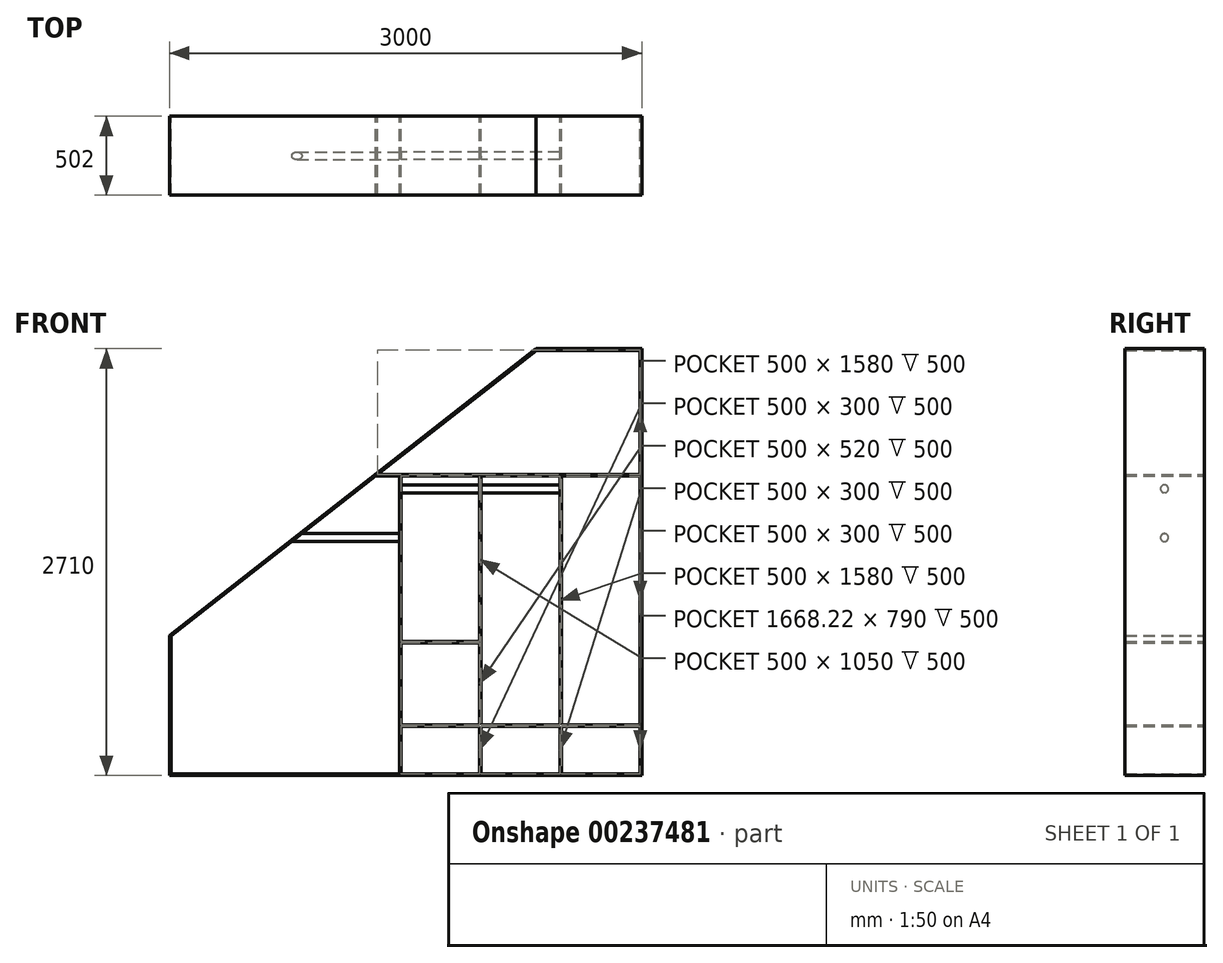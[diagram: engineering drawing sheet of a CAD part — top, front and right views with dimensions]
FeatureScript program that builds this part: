
annotation { "Feature Type Name" : "Feature", "Feature Type Description" : "" }
export const myFeature = defineFeature(function(context is Context, id is Id, definition is map)
    precondition{}
    {
        {
            var Q0;
            Q0=qCreatedBy(makeId("Front.planeOp"),FACE);
            var sketch = newSketch(context, id + "F0", { "sketchPlane" : qUnion([Q0])});
            skLineSegment(sketch, "E0", {"start": v(0, 0) * mm, "end": v(3000, 0) * mm});
            skLineSegment(sketch, "E1", {"start": v(3000, 0) * mm, "end": v(3000, 2710) * mm});
            skLineSegment(sketch, "E2", {"start": v(3000, 2710) * mm, "end": v(2329.5, 2710) * mm});
            skLineSegment(sketch, "E3", {"start": v(2329.5, 2710) * mm, "end": v(0, 890) * mm});
            skLineSegment(sketch, "E4", {"start": v(0, 890) * mm, "end": v(0, 0) * mm});
            skLineSegment(sketch, "E5.0", {"start": v(10, 885.12) * mm, "end": v(10, 10) * mm});
            skLineSegment(sketch, "E5.1", {"start": v(2332.94, 2700) * mm, "end": v(1321.78, 1910) * mm});
            skLineSegment(sketch, "E5.2", {"start": v(10, 10) * mm, "end": v(1460, 10) * mm});
            skLineSegment(sketch, "E5.3", {"start": v(2990, 10) * mm, "end": v(2990, 1900) * mm});
            skLineSegment(sketch, "E5.4", {"start": v(2990, 2700) * mm, "end": v(2332.94, 2700) * mm});
            skLineSegment(sketch, "E6", {"start": v(1036.75, 0) * mm, "end": v(1036.75, 1700) * mm, "construction": true});
            skLineSegment(sketch, "E7", {"start": v(1321.78, 1910) * mm, "end": v(2990, 1910) * mm});
            skLineSegment(sketch, "E8", {"start": v(2990, 1900) * mm, "end": v(2490, 1900) * mm});
            skLineSegment(sketch, "E9", {"start": v(2490, 1900) * mm, "end": v(2490, 320) * mm});
            skLineSegment(sketch, "E10", {"start": v(2480, 10) * mm, "end": v(2480, 310) * mm});
            skLineSegment(sketch, "E11", {"start": v(1970, 1900) * mm, "end": v(1970, 850) * mm});
            skLineSegment(sketch, "E12", {"start": v(1980, 1900) * mm, "end": v(1980, 320) * mm});
            skLineSegment(sketch, "E13", {"start": v(1470, 1900) * mm, "end": v(1470, 850) * mm});
            skLineSegment(sketch, "E14", {"start": v(1460, 1900) * mm, "end": v(1460, 10) * mm});
            skLineSegment(sketch, "E15.bottom", {"start": v(1470, 320) * mm, "end": v(1970, 320) * mm});
            skLineSegment(sketch, "E15.top", {"start": v(1470, 310) * mm, "end": v(1970, 310) * mm});
            skLineSegment(sketch, "E15.left", {"start": v(1470, 320) * mm, "end": v(1470, 310) * mm});
            skLineSegment(sketch, "E16.bottom", {"start": v(1470, 850) * mm, "end": v(1970, 850) * mm});
            skLineSegment(sketch, "E16.top", {"start": v(1470, 840) * mm, "end": v(1970, 840) * mm});
            skLineSegment(sketch, "E17.trimOffspring", {"start": v(1308.98, 1900) * mm, "end": v(10, 885.12) * mm});
            skLineSegment(sketch, "E18.trimOffspring", {"start": v(1460, 1900) * mm, "end": v(1308.98, 1900) * mm});
            skLineSegment(sketch, "E19.trimOffspring", {"start": v(1970, 1900) * mm, "end": v(1470, 1900) * mm});
            skLineSegment(sketch, "E20.trimOffspring", {"start": v(2480, 1900) * mm, "end": v(1980, 1900) * mm});
            skLineSegment(sketch, "E21.trimOffspring", {"start": v(2990, 1910) * mm, "end": v(2990, 2700) * mm});
            skLineSegment(sketch, "E22.trimOffspring", {"start": v(1470, 840) * mm, "end": v(1470, 10) * mm});
            skLineSegment(sketch, "E23.trimOffspring", {"start": v(1970, 840) * mm, "end": v(1970, 320) * mm});
            skLineSegment(sketch, "E24.trimOffspring", {"start": v(2490, 310) * mm, "end": v(2490, 10) * mm});
            skLineSegment(sketch, "E25.trimOffspring", {"start": v(2490, 320) * mm, "end": v(2990, 320) * mm});
            skLineSegment(sketch, "E26.trimOffspring", {"start": v(2480, 320) * mm, "end": v(2480, 1900) * mm});
            skLineSegment(sketch, "E27.trimOffspring", {"start": v(2490, 310) * mm, "end": v(2990, 310) * mm});
            skLineSegment(sketch, "E28.trimOffspring", {"start": v(1980, 320) * mm, "end": v(2480, 320) * mm});
            skLineSegment(sketch, "E29.trimOffspring", {"start": v(1980, 310) * mm, "end": v(2480, 310) * mm});
            skLineSegment(sketch, "E30.trimOffspring", {"start": v(1970, 310) * mm, "end": v(1970, 10) * mm});
            skLineSegment(sketch, "E31.trimOffspring", {"start": v(1980, 310) * mm, "end": v(1980, 10) * mm});
            skLineSegment(sketch, "E32.trimOffspring", {"start": v(2490, 10) * mm, "end": v(2990, 10) * mm});
            skLineSegment(sketch, "E33.trimOffspring", {"start": v(1980, 10) * mm, "end": v(2480, 10) * mm});
            skLineSegment(sketch, "E34.trimOffspring", {"start": v(1470, 10) * mm, "end": v(1970, 10) * mm});
            skSolve(sketch);
        }
        {
            var Q0;
            Q0=makeQuery(id+"F0.imprint","IMPRINT",FACE,{"disambiguationData":[TD([[makeQuery(id+"F0.imprint","IMPRINT",EDGE,{"derivedFrom":sQuery(id+"F0.wireOp",EDGE,"E0")}),1.0]])]});
            extrude(context, id + "F1", {"entities" : qUnion([Q0]), "depth" : 500 * mm});
        }
        {
            var Q0;
            Q0=makeQuery(id+"F0.imprint","IMPRINT",FACE,{"disambiguationData":[TD([[makeQuery(id+"F0.imprint","IMPRINT",EDGE,{"derivedFrom":sQuery(id+"F0.wireOp",EDGE,"E5.0")}),1.0]])]});
            var Q1;
            Q1=makeQuery(id+"F0.imprint","IMPRINT",FACE,{"disambiguationData":[TD([[makeQuery(id+"F0.imprint","IMPRINT",EDGE,{"derivedFrom":sQuery(id+"F0.wireOp",EDGE,"E0")}),1.0]])]});
            var Q2;
            {var subQ3=sQuery(id+"F0.wireOp",EDGE,"E9");Q2=makeQuery(id+"F0.imprint","IMPRINT",FACE,{"disambiguationData":[TD([[makeQuery(id+"F0.imprint","IMPRINT",EDGE,{"derivedFrom":subQ3}),1.0]])]});}
            var Q3;
            {var subQ0=sQuery(id+"F0.wireOp",EDGE,"E5.4");Q3=makeQuery(id+"F0.imprint","IMPRINT",FACE,{"disambiguationData":[TD([[makeQuery(id+"F0.imprint","IMPRINT",EDGE,{"derivedFrom":subQ0}),1.0]])]});}
            var Q4;
            {var subQ0=sQuery(id+"F0.wireOp",EDGE,"E11");Q4=makeQuery(id+"F0.imprint","IMPRINT",FACE,{"disambiguationData":[TD([[makeQuery(id+"F0.imprint","IMPRINT",EDGE,{"derivedFrom":subQ0}),1.0]])]});}
            var Q5;
            Q5=makeQuery(id+"F0.imprint","IMPRINT",FACE,{"disambiguationData":[TD([[makeQuery(id+"F0.imprint","IMPRINT",EDGE,{"derivedFrom":sQuery(id+"F0.wireOp",EDGE,"E7")}),-1.0]])]});
            var Q6;
            {var subQ0=sQuery(id+"F0.wireOp",EDGE,"E9");Q6=makeQuery(id+"F0.imprint","IMPRINT",FACE,{"disambiguationData":[TD([[makeQuery(id+"F0.imprint","IMPRINT",EDGE,{"derivedFrom":subQ0}),-1.0]])]});}
            var Q7;
            {var subQ0=sQuery(id+"F0.wireOp",EDGE,"E11");Q7=makeQuery(id+"F0.imprint","IMPRINT",FACE,{"disambiguationData":[TD([[makeQuery(id+"F0.imprint","IMPRINT",EDGE,{"derivedFrom":subQ0}),-1.0]])]});}
            var Q8;
            {var subQ0=sQuery(id+"F0.wireOp",EDGE,"E13");Q8=makeQuery(id+"F0.imprint","IMPRINT",FACE,{"disambiguationData":[TD([[makeQuery(id+"F0.imprint","IMPRINT",EDGE,{"derivedFrom":subQ0}),-1.0]])]});}
            var Q9;
            Q9=makeQuery(id+"F0.imprint","IMPRINT",FACE,{"disambiguationData":[TD([[makeQuery(id+"F0.imprint","IMPRINT",EDGE,{"derivedFrom":sQuery(id+"F0.wireOp",EDGE,"E12")}),1.0]])]});
            var Q10;
            Q10=makeQuery(id+"F0.imprint","IMPRINT",FACE,{"disambiguationData":[TD([[makeQuery(id+"F0.imprint","IMPRINT",EDGE,{"derivedFrom":sQuery(id+"F0.wireOp",EDGE,"E24.trimOffspring")}),1.0]])]});
            var Q11;
            Q11=makeQuery(id+"F0.imprint","IMPRINT",FACE,{"disambiguationData":[TD([[makeQuery(id+"F0.imprint","IMPRINT",EDGE,{"derivedFrom":sQuery(id+"F0.wireOp",EDGE,"E10")}),1.0]])]});
            var Q12;
            {var subQ0=sQuery(id+"F0.wireOp",EDGE,"E15.top");Q12=makeQuery(id+"F0.imprint","IMPRINT",FACE,{"disambiguationData":[TD([[makeQuery(id+"F0.imprint","IMPRINT",EDGE,{"derivedFrom":subQ0}),-1.0]])]});}
            var Q13;
            {var subQ0=sQuery(id+"F0.wireOp",EDGE,"E15.bottom");Q13=makeQuery(id+"F0.imprint","IMPRINT",FACE,{"disambiguationData":[TD([[makeQuery(id+"F0.imprint","IMPRINT",EDGE,{"derivedFrom":subQ0}),1.0]])]});}
            extrude(context, id + "F2", {"entities" : qUnion([Q0, Q1, Q2, Q3, Q4, Q5, Q6, Q7, Q8, Q9, Q10, Q11, Q12, Q13]), "operationType" : NewBodyOperationType.ADD, "oppositeDirection" : true, "depth" : 2 * mm});
        }
        {
            var Q0;
            {var subQ0=sQuery(id+"F0.wireOp",EDGE,"E13");Q0=makeQuery(id+"F1.opExtrude","SWEPT_FACE",FACE,{"disambiguationData":[OSD([subQ0]),TDD([makeQuery(id+"F0.imprint","IMPRINT",EDGE,{"disambiguationData":[TD([[makeQuery(id+"F0.imprint","INTERSECT",VERTEX,{"derivedFrom":[sQuery(id+"F0.wireOp",EDGE,"E8"),subQ0]}),-1.0]])],"derivedFrom":subQ0})])]});}
            var sketch = newSketch(context, id + "F3", { "sketchPlane" : qUnion([Q0])});
            skCircle(sketch, "E35", {"center": v(-250, 1820) * mm, "radius": 25 * mm});
            skSolve(sketch);
        }
        {
            var Q0;
            Q0=makeQuery(id+"F3.imprint","IMPRINT",FACE,{"disambiguationData":[TD([[makeQuery(id+"F3.imprint","IMPRINT",EDGE,{"derivedFrom":sQuery(id+"F3.wireOp",EDGE,"E35")}),1.0]])]});
            var Q1;
            {var subQ0=sQuery(id+"F0.wireOp",EDGE,"E10");Q1=makeQuery(id+"F1.opExtrude","SWEPT_FACE",FACE,{"disambiguationData":[OSD([subQ0]),TDD([makeQuery(id+"F0.imprint","IMPRINT",EDGE,{"disambiguationData":[TD([[makeQuery(id+"F0.imprint","INTERSECT",VERTEX,{"derivedFrom":[sQuery(id+"F0.wireOp",EDGE,"E8"),subQ0]}),1.0]])],"derivedFrom":subQ0})])]});}
            extrude(context, id + "F4", {"entities" : qUnion([Q0]), "operationType" : NewBodyOperationType.ADD, "endBound" : BoundingType.UP_TO_SURFACE, "endBoundEntityFace" : qUnion([Q1]), "depth" : 25 * mm});
        }
        {
            var Q0;
            Q0=makeQuery(id+"F1.opExtrude","SWEPT_FACE",FACE,{"disambiguationData":[OSD([sQuery(id+"F0.wireOp",EDGE,"E14")])]});
            var sketch = newSketch(context, id + "F5", { "sketchPlane" : qUnion([Q0])});
            skCircle(sketch, "E36", {"center": v(250, 1510) * mm, "radius": 25 * mm});
            skSolve(sketch);
        }
        {
            var Q0;
            Q0=qSketchRegion(id+"F5",true);
            var Q1;
            {var subQ0=sQuery(id+"F0.wireOp",EDGE,"E5.1");Q1=makeQuery(id+"F1.opExtrude","SWEPT_FACE",FACE,{"disambiguationData":[OSD([subQ0]),TDD([makeQuery(id+"F0.imprint","IMPRINT",EDGE,{"disambiguationData":[TD([[makeQuery(id+"F0.imprint","INTERSECT",VERTEX,{"derivedFrom":[sQuery(id+"F0.wireOp",EDGE,"E5.0"),subQ0]}),1.0]])],"derivedFrom":subQ0})])]});}
            extrude(context, id + "F6", {"entities" : qUnion([Q0]), "operationType" : NewBodyOperationType.ADD, "endBound" : BoundingType.UP_TO_SURFACE, "endBoundEntityFace" : qUnion([Q1]), "depth" : 25 * mm});
        }
    });
